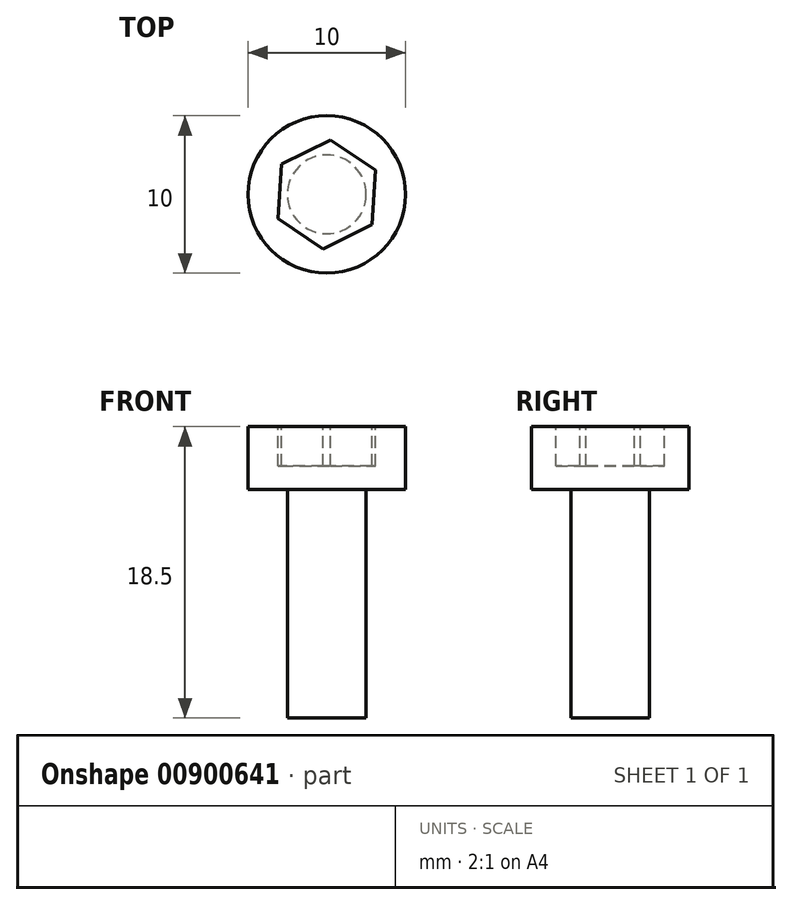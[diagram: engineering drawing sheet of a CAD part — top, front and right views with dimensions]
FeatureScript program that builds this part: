
annotation { "Feature Type Name" : "Feature", "Feature Type Description" : "" }
export const myFeature = defineFeature(function(context is Context, id is Id, definition is map)
    precondition{}
    {
        {
            var Q0;
            Q0=qCreatedBy(makeId("Front.planeOp"),FACE);
            var sketch = newSketch(context, id + "F0", { "sketchPlane" : qUnion([Q0])});
            skLineSegment(sketch, "E0.bottom", {"start": v(3.17, 8.98) * mm, "end": v(5.67, 8.98) * mm});
            skLineSegment(sketch, "E0.top", {"start": v(3.17, -9.52) * mm, "end": v(5.67, -9.52) * mm});
            skLineSegment(sketch, "E0.left", {"start": v(3.17, 8.98) * mm, "end": v(3.17, -9.52) * mm});
            skLineSegment(sketch, "E0.right", {"start": v(5.67, 4.98) * mm, "end": v(5.67, -9.52) * mm});
            skLineSegment(sketch, "E1.bottom", {"start": v(5.67, 8.98) * mm, "end": v(8.17, 8.98) * mm});
            skLineSegment(sketch, "E1.top", {"start": v(5.67, 4.98) * mm, "end": v(8.17, 4.98) * mm});
            skLineSegment(sketch, "E1.right", {"start": v(8.17, 8.98) * mm, "end": v(8.17, 4.98) * mm});
            skLineSegment(sketch, "E2", {"start": v(3.17, 14.93) * mm, "end": v(3.17, -12.6) * mm, "construction": true});
            skSolve(sketch);
        }
        {
            var Q0;
            Q0=makeQuery(id+"F0.imprint","IMPRINT",FACE,{"disambiguationData":[TD([[makeQuery(id+"F0.imprint","IMPRINT",EDGE,{"derivedFrom":sQuery(id+"F0.wireOp",EDGE,"E0.bottom")}),-1.0]])]});
            var Q1;
            Q1=sQuery(id+"F0.wireOp",EDGE,"E2");
            revolve(context, id + "F1", {"surfaceOperationType" : NewSurfaceOperationType.NEW, "entities" : qUnion([Q0]), "axis" : qUnion([Q1]), "revolveType" : RevolveType.FULL});
        }
        {
            var Q0;
            Q0=makeQuery(id+"F1.opRevolve","SWEPT_FACE",FACE,{"disambiguationData":[OSD([sQuery(id+"F0.wireOp",EDGE,"E0.bottom"),sQuery(id+"F0.wireOp",EDGE,"E1.bottom")])]});
            var sketch = newSketch(context, id + "F2", { "sketchPlane" : qUnion([Q0])});
            skCircle(sketch, "E3.cCircle", {"center": v(3.17, 0) * mm, "radius": 3 * mm, "construction": true});
            skLineSegment(sketch, "E3.0", {"start": v(6.05, -1.93) * mm, "end": v(2.94, -3.46) * mm});
            skLineSegment(sketch, "E3.1", {"start": v(2.94, -3.46) * mm, "end": v(0.06, -1.53) * mm});
            skLineSegment(sketch, "E3.2", {"start": v(0.06, -1.53) * mm, "end": v(0.29, 1.93) * mm});
            skLineSegment(sketch, "E3.3", {"start": v(0.29, 1.93) * mm, "end": v(3.4, 3.46) * mm});
            skLineSegment(sketch, "E3.4", {"start": v(3.4, 3.46) * mm, "end": v(6.28, 1.53) * mm});
            skLineSegment(sketch, "E3.5", {"start": v(6.28, 1.53) * mm, "end": v(6.05, -1.93) * mm});
            skPoint(sketch, "E3.0.midPoint", {"position": v(4.5, -2.7) * mm});
            skSolve(sketch);
        }
        {
            var Q0;
            Q0=makeQuery(id+"F2.imprint","IMPRINT",FACE,{"disambiguationData":[TD([[makeQuery(id+"F2.imprint","IMPRINT",EDGE,{"derivedFrom":sQuery(id+"F2.wireOp",EDGE,"E3.0")}),-1.0]])]});
            extrude(context, id + "F3", {"entities" : qUnion([Q0]), "operationType" : NewBodyOperationType.REMOVE, "oppositeDirection" : true, "depth" : 2.5 * mm, "offsetDistance" : 25 * mm});
        }
    });
